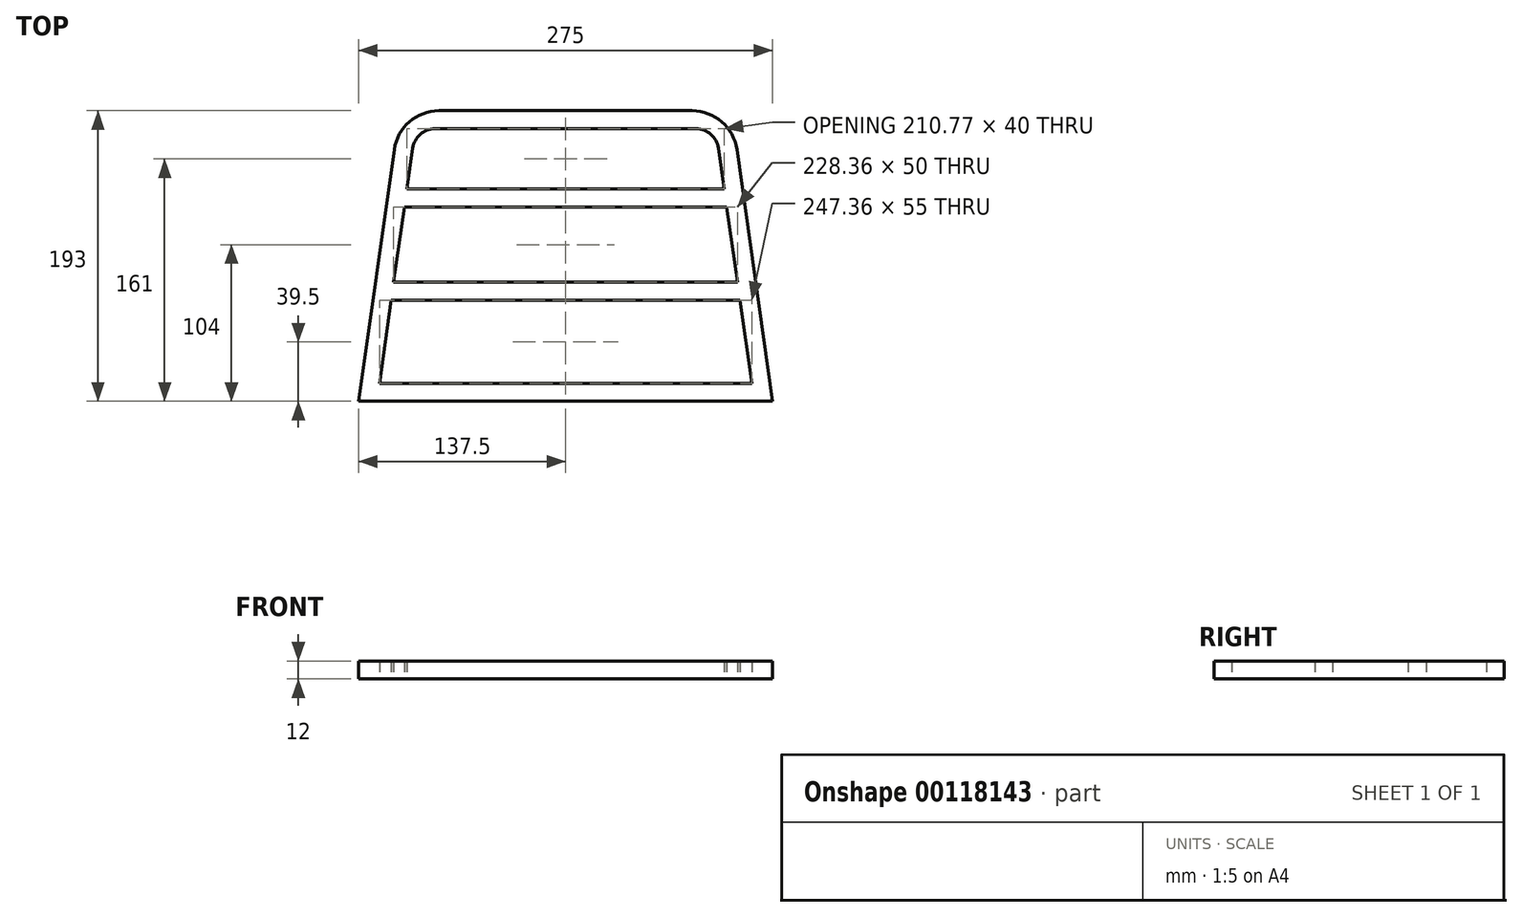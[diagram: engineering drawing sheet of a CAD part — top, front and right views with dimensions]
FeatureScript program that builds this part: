
annotation { "Feature Type Name" : "Feature", "Feature Type Description" : "" }
export const myFeature = defineFeature(function(context is Context, id is Id, definition is map)
    precondition{}
    {
        {
            var Q0;
            Q0=qCreatedBy(makeId("Top.planeOp"),FACE);
            var sketch = newSketch(context, id + "F0", { "sketchPlane" : qUnion([Q0])});
            skLineSegment(sketch, "E0", {"start": v(0, 0) * mm, "end": v(275, 0) * mm});
            skLineSegment(sketch, "E1.0", {"start": v(1.7, 12) * mm, "end": v(137.5, 12) * mm});
            skLineSegment(sketch, "E2.0", {"start": v(18.3, 129) * mm, "end": v(137.5, 129) * mm});
            skLineSegment(sketch, "E3.0", {"start": v(20, 141) * mm, "end": v(137.5, 141) * mm});
            skLineSegment(sketch, "E4.0", {"start": v(25.66, 181) * mm, "end": v(137.5, 181) * mm});
            skLineSegment(sketch, "E5.0", {"start": v(27.37, 193) * mm, "end": v(137.5, 193) * mm});
            skPoint(sketch, "E6", {"position": v(137.5, 0) * mm});
            skLineSegment(sketch, "E7", {"start": v(137.5, 0) * mm, "end": v(137.5, 214.03) * mm, "construction": true});
            skPoint(sketch, "E8", {"position": v(137.5, 67) * mm});
            skLineSegment(sketch, "E9", {"start": v(137.5, 67) * mm, "end": v(9.5, 67) * mm});
            skLineSegment(sketch, "E10.0", {"start": v(137.5, 79) * mm, "end": v(11.2, 79) * mm});
            skLineSegment(sketch, "E11", {"start": v(0, 0) * mm, "end": v(27.37, 193) * mm});
            skLineSegment(sketch, "E12.MirrorCS", {"start": v(275, 0) * mm, "end": v(247.63, 193) * mm});
            skLineSegment(sketch, "E13.MirrorCS", {"start": v(249.34, 181) * mm, "end": v(137.5, 181) * mm});
            skLineSegment(sketch, "E14.MirrorCS", {"start": v(247.63, 193) * mm, "end": v(137.5, 193) * mm});
            skLineSegment(sketch, "E15.MirrorCS", {"start": v(255, 141) * mm, "end": v(137.5, 141) * mm});
            skLineSegment(sketch, "E16.MirrorCS", {"start": v(256.7, 129) * mm, "end": v(137.5, 129) * mm});
            skLineSegment(sketch, "E17.MirrorCS", {"start": v(137.5, 79) * mm, "end": v(263.8, 79) * mm});
            skLineSegment(sketch, "E18.MirrorCS", {"start": v(137.5, 67) * mm, "end": v(265.5, 67) * mm});
            skLineSegment(sketch, "E19.0", {"start": v(12.12, 0) * mm, "end": v(39.49, 193) * mm});
            skLineSegment(sketch, "E20.MirrorCS", {"start": v(262.88, 0) * mm, "end": v(235.51, 193) * mm});
            skLineSegment(sketch, "E21.MirrorCS", {"start": v(273.3, 12) * mm, "end": v(137.5, 12) * mm});
            skSolve(sketch);
        }
        {
            var Q0;
            {var subQ5=sQuery(id+"F0.wireOp",EDGE,"E13.MirrorCS");var subQ6=sQuery(id+"F0.wireOp",EDGE,"E4.0");var subQ7=makeQuery(id+"F0.imprint","INTERSECT",VERTEX,{"derivedFrom":[subQ6,subQ5]});Q0=makeQuery(id+"F0.imprint","IMPRINT",FACE,{"disambiguationData":[TD([[makeQuery(id+"F0.imprint","IMPRINT",EDGE,{"disambiguationData":[TD([[subQ7,1.0]])],"derivedFrom":subQ6}),1.0]])]});}
            var Q1;
            {var subQ0=sQuery(id+"F0.wireOp",EDGE,"E11");var subQ1=sQuery(id+"F0.wireOp",EDGE,"E4.0");var subQ2=makeQuery(id+"F0.imprint","INTERSECT",VERTEX,{"derivedFrom":[subQ1,subQ0]});Q1=makeQuery(id+"F0.imprint","IMPRINT",FACE,{"disambiguationData":[TD([[makeQuery(id+"F0.imprint","IMPRINT",EDGE,{"disambiguationData":[TD([[subQ2,-1.0]])],"derivedFrom":subQ1}),1.0]])]});}
            var Q2;
            {var subQ0=sQuery(id+"F0.wireOp",EDGE,"E11");var subQ1=sQuery(id+"F0.wireOp",EDGE,"E3.0");var subQ2=makeQuery(id+"F0.imprint","INTERSECT",VERTEX,{"derivedFrom":[subQ1,subQ0]});Q2=makeQuery(id+"F0.imprint","IMPRINT",FACE,{"disambiguationData":[TD([[makeQuery(id+"F0.imprint","IMPRINT",EDGE,{"disambiguationData":[TD([[subQ2,-1.0]])],"derivedFrom":subQ1}),1.0]])]});}
            var Q3;
            {var subQ0=sQuery(id+"F0.wireOp",EDGE,"E11");var subQ1=sQuery(id+"F0.wireOp",EDGE,"E2.0");var subQ2=makeQuery(id+"F0.imprint","INTERSECT",VERTEX,{"derivedFrom":[subQ1,subQ0]});Q3=makeQuery(id+"F0.imprint","IMPRINT",FACE,{"disambiguationData":[TD([[makeQuery(id+"F0.imprint","IMPRINT",EDGE,{"disambiguationData":[TD([[subQ2,-1.0]])],"derivedFrom":subQ1}),1.0]])]});}
            var Q4;
            {var subQ0=sQuery(id+"F0.wireOp",EDGE,"E13.MirrorCS");var subQ1=sQuery(id+"F0.wireOp",EDGE,"E12.MirrorCS");var subQ2=makeQuery(id+"F0.imprint","INTERSECT",VERTEX,{"derivedFrom":[subQ1,subQ0]});Q4=makeQuery(id+"F0.imprint","IMPRINT",FACE,{"disambiguationData":[TD([[makeQuery(id+"F0.imprint","IMPRINT",EDGE,{"disambiguationData":[TD([[subQ2,1.0]])],"derivedFrom":subQ1}),1.0]])]});}
            var Q5;
            {var subQ0=sQuery(id+"F0.wireOp",EDGE,"E14.MirrorCS");var subQ1=sQuery(id+"F0.wireOp",EDGE,"E12.MirrorCS");var subQ2=makeQuery(id+"F0.imprint","INTERSECT",VERTEX,{"derivedFrom":[subQ1,subQ0]});Q5=makeQuery(id+"F0.imprint","IMPRINT",FACE,{"disambiguationData":[TD([[makeQuery(id+"F0.imprint","IMPRINT",EDGE,{"disambiguationData":[TD([[subQ2,1.0]])],"derivedFrom":subQ1}),1.0]])]});}
            var Q6;
            {var subQ0=sQuery(id+"F0.wireOp",EDGE,"E15.MirrorCS");var subQ1=sQuery(id+"F0.wireOp",EDGE,"E12.MirrorCS");var subQ2=makeQuery(id+"F0.imprint","INTERSECT",VERTEX,{"derivedFrom":[subQ1,subQ0]});Q6=makeQuery(id+"F0.imprint","IMPRINT",FACE,{"disambiguationData":[TD([[makeQuery(id+"F0.imprint","IMPRINT",EDGE,{"disambiguationData":[TD([[subQ2,1.0]])],"derivedFrom":subQ1}),1.0]])]});}
            var Q7;
            {var subQ0=sQuery(id+"F0.wireOp",EDGE,"E16.MirrorCS");var subQ1=sQuery(id+"F0.wireOp",EDGE,"E12.MirrorCS");var subQ2=makeQuery(id+"F0.imprint","INTERSECT",VERTEX,{"derivedFrom":[subQ1,subQ0]});Q7=makeQuery(id+"F0.imprint","IMPRINT",FACE,{"disambiguationData":[TD([[makeQuery(id+"F0.imprint","IMPRINT",EDGE,{"disambiguationData":[TD([[subQ2,1.0]])],"derivedFrom":subQ1}),1.0]])]});}
            var Q8;
            {var subQ0=sQuery(id+"F0.wireOp",EDGE,"E17.MirrorCS");var subQ1=sQuery(id+"F0.wireOp",EDGE,"E12.MirrorCS");var subQ2=makeQuery(id+"F0.imprint","INTERSECT",VERTEX,{"derivedFrom":[subQ1,subQ0]});Q8=makeQuery(id+"F0.imprint","IMPRINT",FACE,{"disambiguationData":[TD([[makeQuery(id+"F0.imprint","IMPRINT",EDGE,{"disambiguationData":[TD([[subQ2,1.0]])],"derivedFrom":subQ1}),1.0]])]});}
            var Q9;
            {var subQ0=sQuery(id+"F0.wireOp",EDGE,"E18.MirrorCS");var subQ1=sQuery(id+"F0.wireOp",EDGE,"E9");var subQ2=makeQuery(id+"F0.imprint","INTERSECT",VERTEX,{"derivedFrom":[subQ1,subQ0]});Q9=makeQuery(id+"F0.imprint","IMPRINT",FACE,{"disambiguationData":[TD([[makeQuery(id+"F0.imprint","IMPRINT",EDGE,{"disambiguationData":[TD([[subQ2,-1.0]])],"derivedFrom":subQ1}),-1.0]])]});}
            var Q10;
            {var subQ0=sQuery(id+"F0.wireOp",EDGE,"E18.MirrorCS");var subQ1=sQuery(id+"F0.wireOp",EDGE,"E12.MirrorCS");var subQ2=makeQuery(id+"F0.imprint","INTERSECT",VERTEX,{"derivedFrom":[subQ1,subQ0]});Q10=makeQuery(id+"F0.imprint","IMPRINT",FACE,{"disambiguationData":[TD([[makeQuery(id+"F0.imprint","IMPRINT",EDGE,{"disambiguationData":[TD([[subQ2,1.0]])],"derivedFrom":subQ1}),1.0]])]});}
            var Q11;
            {var subQ0=sQuery(id+"F0.wireOp",EDGE,"E12.MirrorCS");var subQ1=sQuery(id+"F0.wireOp",EDGE,"E0");var subQ2=makeQuery(id+"F0.imprint","INTERSECT",VERTEX,{"derivedFrom":[subQ1,subQ0]});Q11=makeQuery(id+"F0.imprint","IMPRINT",FACE,{"disambiguationData":[TD([[makeQuery(id+"F0.imprint","IMPRINT",EDGE,{"disambiguationData":[TD([[subQ2,1.0]])],"derivedFrom":subQ1}),1.0]])]});}
            var Q12;
            {var subQ0=sQuery(id+"F0.wireOp",EDGE,"E19.0");var subQ1=sQuery(id+"F0.wireOp",EDGE,"E0");var subQ2=makeQuery(id+"F0.imprint","INTERSECT",VERTEX,{"derivedFrom":[subQ1,subQ0]});Q12=makeQuery(id+"F0.imprint","IMPRINT",FACE,{"disambiguationData":[TD([[makeQuery(id+"F0.imprint","IMPRINT",EDGE,{"disambiguationData":[TD([[subQ2,-1.0]])],"derivedFrom":subQ1}),1.0]])]});}
            var Q13;
            {var subQ0=sQuery(id+"F0.wireOp",EDGE,"E11");var subQ1=sQuery(id+"F0.wireOp",EDGE,"E0");var subQ2=makeQuery(id+"F0.imprint","INTERSECT",VERTEX,{"derivedFrom":[subQ1,subQ0]});Q13=makeQuery(id+"F0.imprint","IMPRINT",FACE,{"disambiguationData":[TD([[makeQuery(id+"F0.imprint","IMPRINT",EDGE,{"disambiguationData":[TD([[subQ2,-1.0]])],"derivedFrom":subQ1}),1.0]])]});}
            var Q14;
            {var subQ0=sQuery(id+"F0.wireOp",EDGE,"E11");var subQ1=sQuery(id+"F0.wireOp",EDGE,"E1.0");var subQ2=makeQuery(id+"F0.imprint","INTERSECT",VERTEX,{"derivedFrom":[subQ1,subQ0]});Q14=makeQuery(id+"F0.imprint","IMPRINT",FACE,{"disambiguationData":[TD([[makeQuery(id+"F0.imprint","IMPRINT",EDGE,{"disambiguationData":[TD([[subQ2,-1.0]])],"derivedFrom":subQ1}),1.0]])]});}
            var Q15;
            {var subQ0=sQuery(id+"F0.wireOp",EDGE,"E11");var subQ1=sQuery(id+"F0.wireOp",EDGE,"E9");var subQ2=makeQuery(id+"F0.imprint","INTERSECT",VERTEX,{"derivedFrom":[subQ1,subQ0]});Q15=makeQuery(id+"F0.imprint","IMPRINT",FACE,{"disambiguationData":[TD([[makeQuery(id+"F0.imprint","IMPRINT",EDGE,{"disambiguationData":[TD([[subQ2,1.0]])],"derivedFrom":subQ1}),-1.0]])]});}
            var Q16;
            {var subQ0=sQuery(id+"F0.wireOp",EDGE,"E11");var subQ1=sQuery(id+"F0.wireOp",EDGE,"E2.0");var subQ2=makeQuery(id+"F0.imprint","INTERSECT",VERTEX,{"derivedFrom":[subQ1,subQ0]});Q16=makeQuery(id+"F0.imprint","IMPRINT",FACE,{"disambiguationData":[TD([[makeQuery(id+"F0.imprint","IMPRINT",EDGE,{"disambiguationData":[TD([[subQ2,-1.0]])],"derivedFrom":subQ1}),-1.0]])]});}
            var Q17;
            {var subQ0=sQuery(id+"F0.wireOp",EDGE,"E16.MirrorCS");var subQ1=sQuery(id+"F0.wireOp",EDGE,"E2.0");var subQ2=makeQuery(id+"F0.imprint","INTERSECT",VERTEX,{"derivedFrom":[subQ1,subQ0]});Q17=makeQuery(id+"F0.imprint","IMPRINT",FACE,{"disambiguationData":[TD([[makeQuery(id+"F0.imprint","IMPRINT",EDGE,{"disambiguationData":[TD([[subQ2,1.0]])],"derivedFrom":subQ1}),1.0]])]});}
            extrude(context, id + "F1", {"entities" : qUnion([Q0, Q1, Q2, Q3, Q4, Q5, Q6, Q7, Q8, Q9, Q10, Q11, Q12, Q13, Q14, Q15, Q16, Q17]), "depth" : 12 * mm});
        }
        {
            var Q0;
            Q0=makeQuery(id+"F1.opExtrude","SWEPT_EDGE",EDGE,{"disambiguationData":[OSD([sQuery(id+"F0.wireOp",EDGE,"E5.0"),sQuery(id+"F0.wireOp",EDGE,"E11")])]});
            var Q1;
            Q1=makeQuery(id+"F1.opExtrude","SWEPT_EDGE",EDGE,{"disambiguationData":[OSD([sQuery(id+"F0.wireOp",EDGE,"E12.MirrorCS"),sQuery(id+"F0.wireOp",EDGE,"E14.MirrorCS")])]});
            fillet(context, id + "F2", {"entities" : qUnion([Q0, Q1]), "radius" : 30 * mm, "tangentPropagation" : true, "allowEdgeOverflow" : false});
        }
        {
            var Q0;
            Q0=makeQuery(id+"F1.opExtrude","SWEPT_EDGE",EDGE,{"disambiguationData":[OSD([sQuery(id+"F0.wireOp",EDGE,"E4.0"),sQuery(id+"F0.wireOp",EDGE,"E19.0")])]});
            var Q1;
            Q1=makeQuery(id+"F1.opExtrude","SWEPT_EDGE",EDGE,{"disambiguationData":[OSD([sQuery(id+"F0.wireOp",EDGE,"E13.MirrorCS"),sQuery(id+"F0.wireOp",EDGE,"E20.MirrorCS")])]});
            fillet(context, id + "F3", {"entities" : qUnion([Q0, Q1]), "radius" : 15 * mm, "tangentPropagation" : true, "allowEdgeOverflow" : false});
        }
    });
